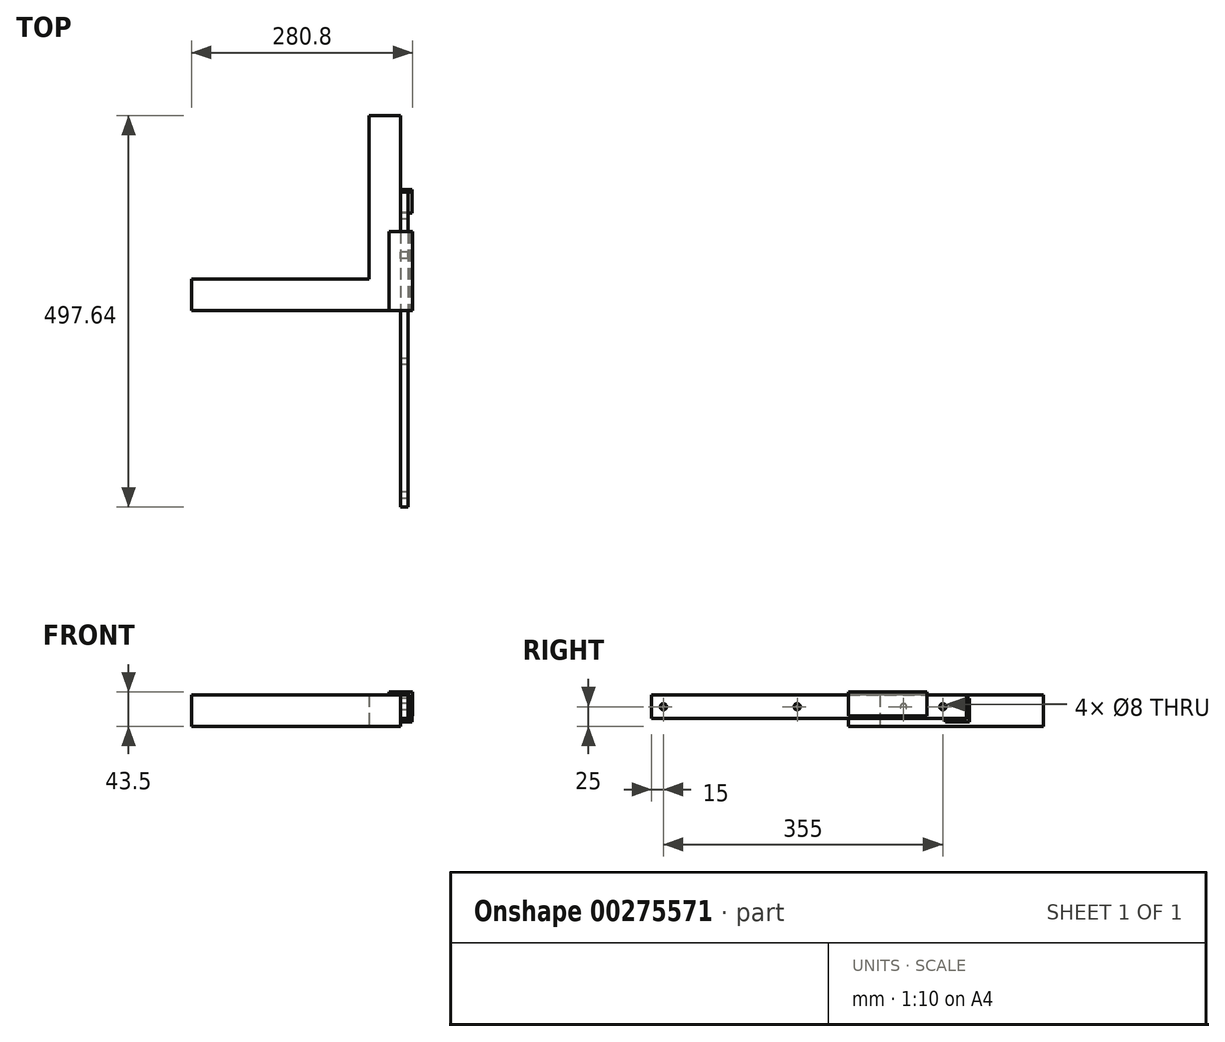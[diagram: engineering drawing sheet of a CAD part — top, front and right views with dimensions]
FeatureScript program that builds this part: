
annotation { "Feature Type Name" : "Feature", "Feature Type Description" : "" }
export const myFeature = defineFeature(function(context is Context, id is Id, definition is map)
    precondition{}
    {
        {
            var Q0;
            Q0=qCreatedBy(makeId("Top.planeOp"),FACE);
            var sketch = newSketch(context, id + "F0", { "sketchPlane" : qUnion([Q0])});
            skLineSegment(sketch, "E0.bottom", {"start": v(0, 0) * mm, "end": v(1240, 0) * mm});
            skLineSegment(sketch, "E0.top", {"start": v(0, 1100) * mm, "end": v(1240, 1100) * mm});
            skLineSegment(sketch, "E0.left", {"start": v(0, 0) * mm, "end": v(0, 1100) * mm});
            skLineSegment(sketch, "E0.right", {"start": v(1240, 0) * mm, "end": v(1240, 1100) * mm});
            skLineSegment(sketch, "E1.bottom", {"start": v(40, 1060) * mm, "end": v(1200, 1060) * mm});
            skLineSegment(sketch, "E1.top", {"start": v(40, 40) * mm, "end": v(1200, 40) * mm});
            skLineSegment(sketch, "E1.left", {"start": v(40, 1060) * mm, "end": v(40, 40) * mm});
            skLineSegment(sketch, "E1.right", {"start": v(1200, 1060) * mm, "end": v(1200, 40) * mm});
            skLineSegment(sketch, "E2", {"start": v(1240, 247.64) * mm, "end": v(1200, 247.64) * mm});
            skLineSegment(sketch, "E3", {"start": v(974.62, 40) * mm, "end": v(974.62, 0) * mm});
            skSolve(sketch);
        }
        {
            var Q0;
            Q0=makeQuery(id+"F0.imprint","IMPRINT",FACE,{"disambiguationData":[TD([[makeQuery(id+"F0.imprint","IMPRINT",EDGE,{"derivedFrom":sQuery(id+"F0.wireOp",EDGE,"E0.bottom")}),1.0]])]});
            extrude(context, id + "F1", {"entities" : qUnion([Q0]), "depth" : 40 * mm});
        }
        {
            var Q0;
            Q0=makeQuery(id+"F1.opExtrude","SWEPT_FACE",FACE,{"disambiguationData":[OSD([sQuery(id+"F0.wireOp",EDGE,"E0.right")])]});
            var sketch = newSketch(context, id + "F2", { "sketchPlane" : qUnion([Q0])});
            skLineSegment(sketch, "E4.bottom", {"start": v(150, 10) * mm, "end": v(-250, 10) * mm});
            skLineSegment(sketch, "E4.top", {"start": v(150, 40) * mm, "end": v(-250, 40) * mm});
            skLineSegment(sketch, "E4.left", {"start": v(150, 10) * mm, "end": v(150, 40) * mm});
            skLineSegment(sketch, "E4.right", {"start": v(-250, 10) * mm, "end": v(-250, 40) * mm});
            skLineSegment(sketch, "E5", {"start": v(150, 25) * mm, "end": v(-250, 25) * mm, "construction": true});
            skLineSegment(sketch, "E6.0", {"start": v(40, 40) * mm, "end": v(40, 0) * mm, "construction": true});
            skCircle(sketch, "E7", {"center": v(120, 25) * mm, "radius": 4 * mm});
            skCircle(sketch, "E8", {"center": v(70, 25) * mm, "radius": 4 * mm});
            skLineSegment(sketch, "E9", {"start": v(40, 9.53) * mm, "end": v(150, 9.53) * mm, "construction": true});
            skLineSegment(sketch, "E10", {"start": v(95, 9.53) * mm, "end": v(95, 40) * mm, "construction": true});
            skCircle(sketch, "E11", {"center": v(-235, 25) * mm, "radius": 4 * mm});
            skCircle(sketch, "E12", {"center": v(-65, 25) * mm, "radius": 4 * mm});
            skSolve(sketch);
        }
        {
            var Q0;
            {var subQ0=sQuery(id+"F2.wireOp",EDGE,"E4.right");Q0=makeQuery(id+"F2.imprint","IMPRINT",FACE,{"disambiguationData":[TD([[makeQuery(id+"F2.imprint","IMPRINT",EDGE,{"derivedFrom":subQ0}),-1.0]])]});}
            var Q1;
            {var subQ0=sQuery(id+"F2.wireOp",EDGE,"E4.left");Q1=makeQuery(id+"F2.imprint","IMPRINT",FACE,{"disambiguationData":[TD([[makeQuery(id+"F2.imprint","IMPRINT",EDGE,{"derivedFrom":subQ0}),1.0]])]});}
            extrude(context, id + "F3", {"entities" : qUnion([Q0, Q1]), "depth" : 10 * mm});
        }
        {
            var Q0;
            Q0=makeQuery(id+"F1.opExtrude","SWEPT_FACE",FACE,{"disambiguationData":[OSD([sQuery(id+"F0.wireOp",EDGE,"E0.bottom")])]});
            var sketch = newSketch(context, id + "F4", { "sketchPlane" : qUnion([Q0])});
            skLineSegment(sketch, "E13.0", {"start": v(1250, 10) * mm, "end": v(1250, 40) * mm, "construction": true});
            skLineSegment(sketch, "E14", {"start": v(1252, 40) * mm, "end": v(1225.42, 40) * mm});
            skLineSegment(sketch, "E15", {"start": v(1225.42, 40) * mm, "end": v(1225.42, 43.5) * mm});
            skLineSegment(sketch, "E16", {"start": v(1225.42, 43.5) * mm, "end": v(1255.42, 43.5) * mm});
            skLineSegment(sketch, "E17", {"start": v(1255.42, 43.5) * mm, "end": v(1255.42, 13.5) * mm});
            skLineSegment(sketch, "E18", {"start": v(1255.42, 13.5) * mm, "end": v(1251.92, 13.5) * mm});
            skLineSegment(sketch, "E19", {"start": v(1251.92, 13.5) * mm, "end": v(1252, 40) * mm});
            skSolve(sketch);
        }
        {
            var Q0;
            {var subQ4=sQuery(id+"F4.wireOp",EDGE,"E15");Q0=makeQuery(id+"F4.imprint","IMPRINT",FACE,{"disambiguationData":[TD([[makeQuery(id+"F4.imprint","IMPRINT",EDGE,{"derivedFrom":subQ4}),-1.0]])]});}
            extrude(context, id + "F5", {"entities" : qUnion([Q0]), "oppositeDirection" : true, "depth" : 100 * mm});
        }
        {
            var Q0;
            Q0=makeQuery(id+"F1.opExtrude","SWEPT_FACE",FACE,{"disambiguationData":[OSD([sQuery(id+"F0.wireOp",EDGE,"E0.right")])]});
            var sketch = newSketch(context, id + "F6", { "sketchPlane" : qUnion([Q0])});
            skLineSegment(sketch, "E20.0", {"start": v(150, 10) * mm, "end": v(150, 40) * mm});
            skLineSegment(sketch, "E21.0", {"start": v(150, 10) * mm, "end": v(-250, 10) * mm, "construction": true});
            skLineSegment(sketch, "E22", {"start": v(150, 10) * mm, "end": v(150, 9) * mm});
            skLineSegment(sketch, "E23", {"start": v(153.5, 5.5) * mm, "end": v(123.5, 5.5) * mm});
            skLineSegment(sketch, "E24", {"start": v(123.5, 5.5) * mm, "end": v(123.5, 9) * mm});
            skLineSegment(sketch, "E25", {"start": v(153.5, 5.5) * mm, "end": v(153.5, 35.5) * mm});
            skLineSegment(sketch, "E26", {"start": v(153.5, 35.5) * mm, "end": v(150, 35.5) * mm});
            skLineSegment(sketch, "E27", {"start": v(123.5, 9) * mm, "end": v(150, 9) * mm});
            skSolve(sketch);
        }
        {
            var Q0;
            {var subQ0=sQuery(id+"F6.wireOp",EDGE,"E22");Q0=makeQuery(id+"F6.imprint","IMPRINT",FACE,{"disambiguationData":[TD([[makeQuery(id+"F6.imprint","IMPRINT",EDGE,{"derivedFrom":subQ0}),1.0]])]});}
            extrude(context, id + "F7", {"entities" : qUnion([Q0]), "depth" : 15 * mm});
        }
    });
